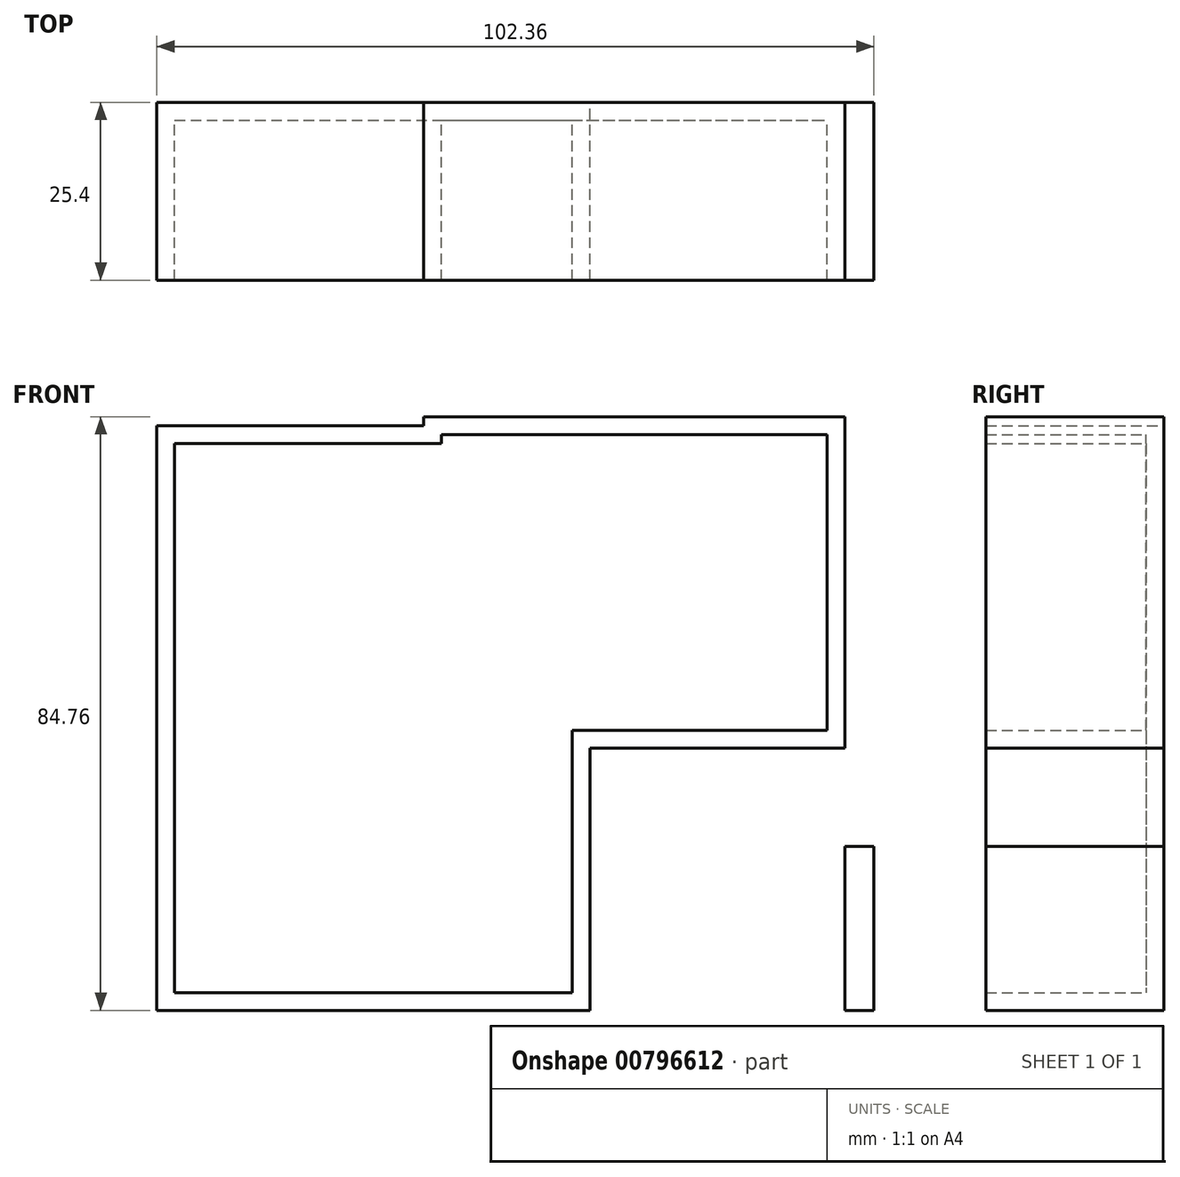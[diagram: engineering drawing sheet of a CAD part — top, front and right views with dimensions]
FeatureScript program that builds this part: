
annotation { "Feature Type Name" : "Feature", "Feature Type Description" : "" }
export const myFeature = defineFeature(function(context is Context, id is Id, definition is map)
    precondition{}
    {
        {
            var Q0;
            Q0=qCreatedBy(makeId("Front.planeOp"),FACE);
            var sketch = newSketch(context, id + "F0", { "sketchPlane" : qUnion([Q0])});
            skLineSegment(sketch, "E0.bottom", {"start": v(-61.8, 83.48) * mm, "end": v(0, 83.48) * mm});
            skLineSegment(sketch, "E0.top", {"start": v(-61.8, 0) * mm, "end": v(0, 0) * mm});
            skLineSegment(sketch, "E0.left", {"start": v(-61.8, 83.48) * mm, "end": v(-61.8, 0) * mm});
            skLineSegment(sketch, "E0.right", {"start": v(0, 83.48) * mm, "end": v(0, 0) * mm});
            skLineSegment(sketch, "E1.bottom", {"start": v(40.55, 0) * mm, "end": v(36.4, 0) * mm});
            skLineSegment(sketch, "E1.top", {"start": v(40.55, 23.42) * mm, "end": v(36.4, 23.42) * mm});
            skLineSegment(sketch, "E1.left", {"start": v(40.55, 0) * mm, "end": v(40.55, 23.42) * mm});
            skLineSegment(sketch, "E1.right", {"start": v(36.4, 0) * mm, "end": v(36.4, 23.42) * mm});
            skLineSegment(sketch, "E2.bottom", {"start": v(-23.7, 37.47) * mm, "end": v(36.4, 37.47) * mm});
            skLineSegment(sketch, "E2.top", {"start": v(-23.7, 84.76) * mm, "end": v(36.4, 84.76) * mm});
            skLineSegment(sketch, "E2.left", {"start": v(-23.7, 37.47) * mm, "end": v(-23.7, 84.76) * mm});
            skLineSegment(sketch, "E2.right", {"start": v(36.4, 37.47) * mm, "end": v(36.4, 84.76) * mm});
            skSolve(sketch);
        }
        {
            var Q0;
            {var subQ0=sQuery(id+"F0.wireOp",EDGE,"E2.top");Q0=makeQuery(id+"F0.imprint","IMPRINT",FACE,{"disambiguationData":[TD([[makeQuery(id+"F0.imprint","IMPRINT",EDGE,{"derivedFrom":subQ0}),-1.0]])]});}
            var Q1;
            Q1=makeQuery(id+"F0.imprint","IMPRINT",FACE,{"disambiguationData":[TD([[makeQuery(id+"F0.imprint","IMPRINT",EDGE,{"derivedFrom":sQuery(id+"F0.wireOp",EDGE,"E1.bottom")}),-1.0]])]});
            var Q2;
            {var subQ1=sQuery(id+"F0.wireOp",EDGE,"E0.top");Q2=makeQuery(id+"F0.imprint","IMPRINT",FACE,{"disambiguationData":[TD([[makeQuery(id+"F0.imprint","IMPRINT",EDGE,{"derivedFrom":subQ1}),1.0]])]});}
            var Q3;
            {var subQ0=sQuery(id+"F0.wireOp",EDGE,"E0.right");var subQ1=sQuery(id+"F0.wireOp",EDGE,"E0.bottom");var subQ2=makeQuery(id+"F0.imprint","INTERSECT",VERTEX,{"derivedFrom":[subQ1,subQ0]});Q3=makeQuery(id+"F0.imprint","IMPRINT",FACE,{"disambiguationData":[TD([[makeQuery(id+"F0.imprint","IMPRINT",EDGE,{"disambiguationData":[TD([[subQ2,1.0]])],"derivedFrom":subQ1}),-1.0]])]});}
            extrude(context, id + "F1", {"entities" : qUnion([Q0, Q1, Q2, Q3]), "depth" : 25.4 * mm, "offsetDistance" : 25.4 * mm});
        }
        {
            var Q0;
            Q0=makeQuery(id+"F1.opExtrude","CAP_FACE",FACE,{"disambiguationData":[OSD([sQuery(id+"F0.wireOp",EDGE,"E0.bottom"),sQuery(id+"F0.wireOp",EDGE,"E0.top"),sQuery(id+"F0.wireOp",EDGE,"E0.left"),sQuery(id+"F0.wireOp",EDGE,"E0.right"),sQuery(id+"F0.wireOp",EDGE,"E2.bottom"),sQuery(id+"F0.wireOp",EDGE,"E2.top"),sQuery(id+"F0.wireOp",EDGE,"E2.left"),sQuery(id+"F0.wireOp",EDGE,"E2.right")])],"isStart":false});
            shell(context, id + "F2", {"entities" : qUnion([Q0]), "thickness" : 2.54 * mm});
        }
    });
